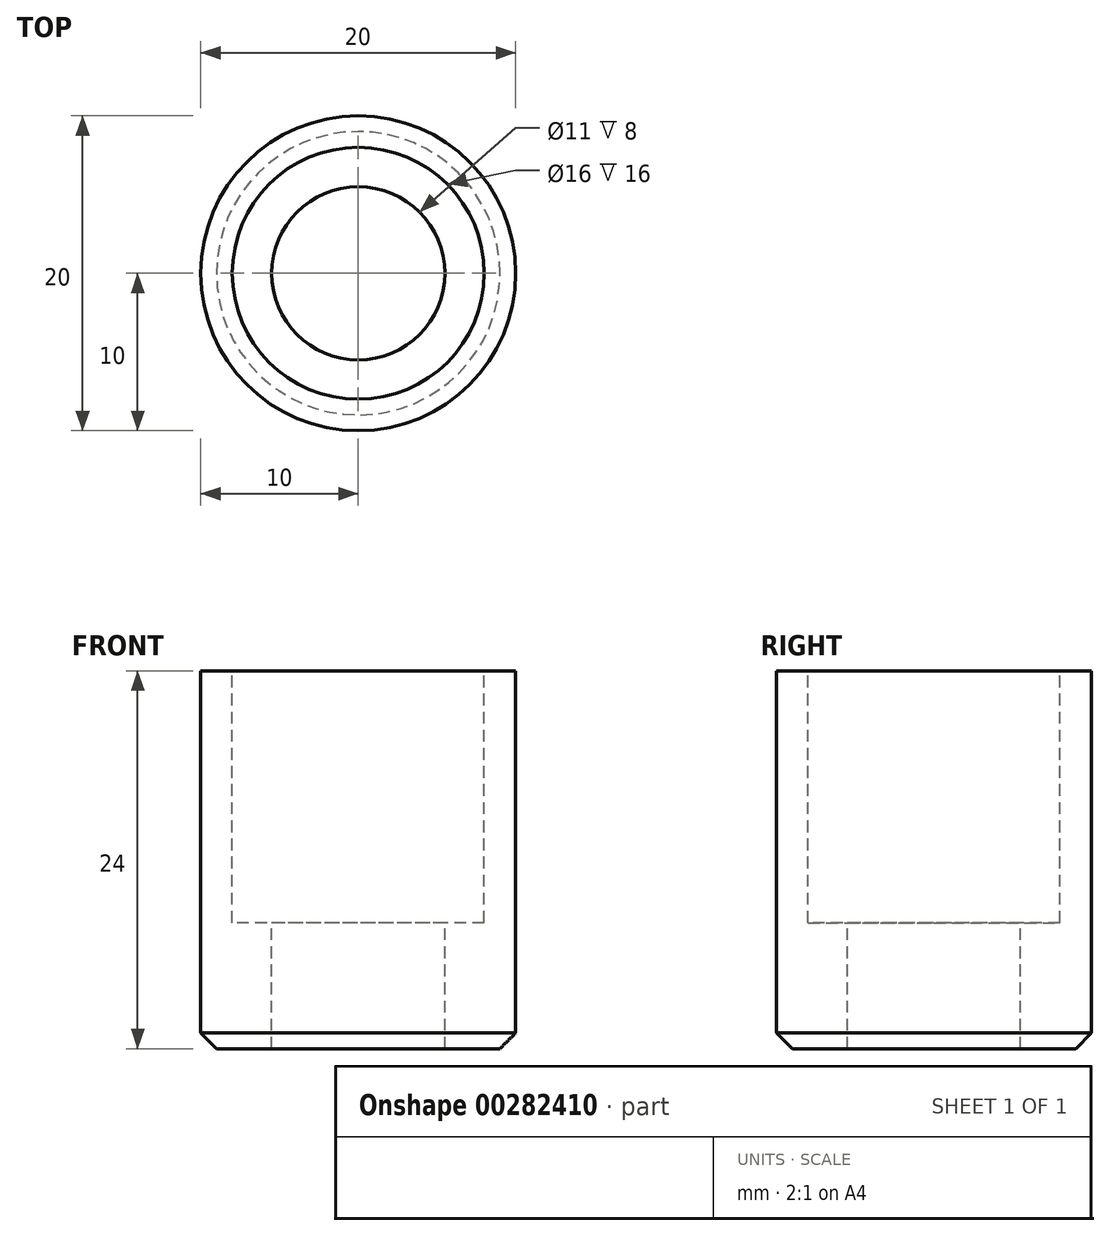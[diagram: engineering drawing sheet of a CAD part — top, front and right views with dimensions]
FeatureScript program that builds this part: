
annotation { "Feature Type Name" : "Feature", "Feature Type Description" : "" }
export const myFeature = defineFeature(function(context is Context, id is Id, definition is map)
    precondition{}
    {
        {
            var Q0;
            Q0=qCreatedBy(makeId("Top.planeOp"),FACE);
            var sketch = newSketch(context, id + "F0", { "sketchPlane" : qUnion([Q0])});
            skCircle(sketch, "E0", {"center": v(0, 0) * mm, "radius": 10 * mm});
            skSolve(sketch);
        }
        {
            var Q0;
            Q0=qSketchRegion(id+"F0",true);
            extrude(context, id + "F1", {"entities" : qUnion([Q0]), "depth" : 24 * mm});
        }
        {
            var Q0;
            Q0=makeQuery(id+"F1.opExtrude","CAP_EDGE",EDGE,{"disambiguationData":[OSD([sQuery(id+"F0.wireOp",EDGE,"E0")])],"isStart":true});
            chamfer(context, id + "F2", {"entities" : qUnion([Q0]), "width" : 1 * mm, "tangentPropagation" : true});
        }
        {
            var Q0;
            Q0=makeQuery(id+"F1.opExtrude","CAP_FACE",FACE,{"disambiguationData":[OSD([sQuery(id+"F0.wireOp",EDGE,"E0")])],"isStart":false});
            var sketch = newSketch(context, id + "F3", { "sketchPlane" : qUnion([Q0])});
            skCircle(sketch, "E1", {"center": v(0, 0) * mm, "radius": 5.5 * mm});
            skSolve(sketch);
        }
        {
            var Q0;
            Q0=qSketchRegion(id+"F3",true);
            extrude(context, id + "F4", {"entities" : qUnion([Q0]), "operationType" : NewBodyOperationType.REMOVE, "endBound" : BoundingType.THROUGH_ALL, "oppositeDirection" : true, "depth" : 25 * mm});
        }
        {
            var Q0;
            Q0=makeQuery(id+"F1.opExtrude","CAP_FACE",FACE,{"disambiguationData":[OSD([sQuery(id+"F0.wireOp",EDGE,"E0")])],"isStart":false});
            var sketch = newSketch(context, id + "F5", { "sketchPlane" : qUnion([Q0])});
            skCircle(sketch, "E2", {"center": v(0, 0) * mm, "radius": 8 * mm});
            skSolve(sketch);
        }
        {
            var Q0;
            Q0=qSketchRegion(id+"F5",true);
            extrude(context, id + "F6", {"entities" : qUnion([Q0]), "operationType" : NewBodyOperationType.REMOVE, "oppositeDirection" : true, "depth" : 16 * mm});
        }
    });
